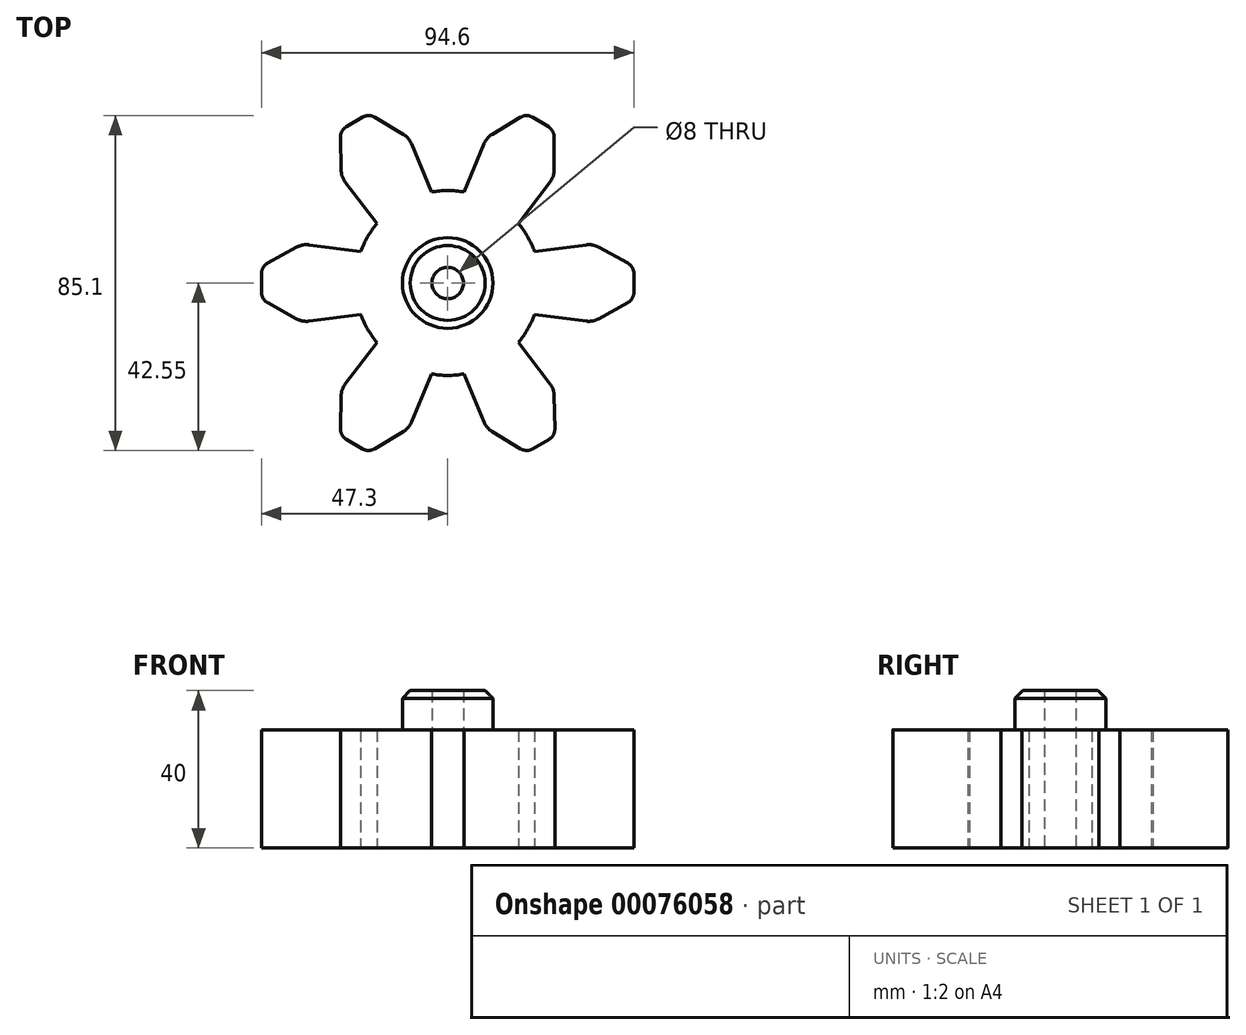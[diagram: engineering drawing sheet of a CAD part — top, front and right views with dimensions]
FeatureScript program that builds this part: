
annotation { "Feature Type Name" : "Feature", "Feature Type Description" : "" }
export const myFeature = defineFeature(function(context is Context, id is Id, definition is map)
    precondition{}
    {
        {
            var Q0;
            Q0=qCreatedBy(makeId("Top.planeOp"),FACE);
            var sketch = newSketch(context, id + "F0", { "sketchPlane" : qUnion([Q0])});
            skCircle(sketch, "E0", {"center": v(0, 0) * mm, "radius": 38.2 * mm, "construction": true});
            skCircle(sketch, "E1", {"center": v(0, 0) * mm, "radius": 50.95 * mm, "construction": true});
            skCircle(sketch, "E2", {"center": v(0, 0) * mm, "radius": 23.47 * mm});
            skLineSegment(sketch, "E3", {"start": v(-50.95, 0) * mm, "end": v(0, 0) * mm});
            skLineSegment(sketch, "E4", {"start": v(0, 0) * mm, "end": v(-25.48, 44.12) * mm, "construction": true});
            skLineSegment(sketch, "E5", {"start": v(0, 0) * mm, "end": v(25.47, 44.12) * mm, "construction": true});
            skLineSegment(sketch, "E6", {"start": v(0, 0) * mm, "end": v(-25.48, -44.12) * mm, "construction": true});
            skLineSegment(sketch, "E7", {"start": v(0, 0) * mm, "end": v(25.48, -44.12) * mm, "construction": true});
            skLineSegment(sketch, "E8", {"start": v(0, 0) * mm, "end": v(50.95, 0) * mm});
            skCircle(sketch, "E9", {"center": v(-19.1, 33.08) * mm, "radius": 10 * mm, "construction": true});
            skCircle(sketch, "E10", {"center": v(-38.2, 0) * mm, "radius": 10 * mm, "construction": true});
            skCircle(sketch, "E11", {"center": v(-19.1, -33.08) * mm, "radius": 10 * mm, "construction": true});
            skCircle(sketch, "E12", {"center": v(19.1, -33.08) * mm, "radius": 10 * mm, "construction": true});
            skCircle(sketch, "E13", {"center": v(38.2, 0) * mm, "radius": 10 * mm, "construction": true});
            skCircle(sketch, "E14", {"center": v(19.1, 33.08) * mm, "radius": 10 * mm, "construction": true});
            skLineSegment(sketch, "E15", {"start": v(0, 0) * mm, "end": v(-44.12, 25.48) * mm, "construction": true});
            skLineSegment(sketch, "E16", {"start": v(0, 0) * mm, "end": v(-44.12, -25.48) * mm, "construction": true});
            skLineSegment(sketch, "E17", {"start": v(-44.12, 25.47) * mm, "end": v(44.12, -25.47) * mm, "construction": true});
            skLineSegment(sketch, "E18", {"start": v(-44.12, -25.47) * mm, "end": v(44.12, 25.47) * mm, "construction": true});
            skLineSegment(sketch, "E19", {"start": v(-27.03, 27) * mm, "end": v(-17.93, 15.14) * mm});
            skLineSegment(sketch, "E20", {"start": v(-9.86, 36.9) * mm, "end": v(-4.15, 23.1) * mm});
            skLineSegment(sketch, "E21", {"start": v(-36.9, 9.91) * mm, "end": v(-22.08, 7.96) * mm});
            skLineSegment(sketch, "E22", {"start": v(-36.9, -9.91) * mm, "end": v(-22.08, -7.96) * mm});
            skLineSegment(sketch, "E23", {"start": v(-27.03, -27) * mm, "end": v(-17.93, -15.14) * mm});
            skLineSegment(sketch, "E24", {"start": v(-9.86, -36.9) * mm, "end": v(-4.15, -23.1) * mm});
            skLineSegment(sketch, "E25", {"start": v(9.86, -36.9) * mm, "end": v(4.15, -23.1) * mm});
            skLineSegment(sketch, "E26", {"start": v(27.03, -27) * mm, "end": v(17.93, -15.14) * mm});
            skLineSegment(sketch, "E27", {"start": v(36.9, -9.91) * mm, "end": v(22.08, -7.96) * mm});
            skLineSegment(sketch, "E28", {"start": v(36.9, 9.91) * mm, "end": v(22.08, 7.96) * mm});
            skLineSegment(sketch, "E29", {"start": v(9.86, 36.9) * mm, "end": v(4.15, 23.1) * mm});
            skLineSegment(sketch, "E30", {"start": v(27.03, 27) * mm, "end": v(17.93, 15.14) * mm});
            skCircle(sketch, "E31", {"center": v(0, 0) * mm, "radius": 4 * mm});
            skCircle(sketch, "E32", {"center": v(-25.48, 44.12) * mm, "radius": 5.53 * mm, "construction": true});
            skLineSegment(sketch, "E33", {"start": v(-27.24, 38.89) * mm, "end": v(-20.06, 43.04) * mm});
            skCircle(sketch, "E34", {"center": v(-50.95, 0) * mm, "radius": 5.53 * mm, "construction": true});
            skCircle(sketch, "E35", {"center": v(-25.48, -44.12) * mm, "radius": 5.53 * mm, "construction": true});
            skCircle(sketch, "E36", {"center": v(25.48, -44.12) * mm, "radius": 5.53 * mm, "construction": true});
            skCircle(sketch, "E37", {"center": v(50.95, 0) * mm, "radius": 5.53 * mm, "construction": true});
            skCircle(sketch, "E38", {"center": v(25.47, 44.12) * mm, "radius": 5.53 * mm, "construction": true});
            skLineSegment(sketch, "E39", {"start": v(-27.24, 38.89) * mm, "end": v(-27.03, 27) * mm});
            skLineSegment(sketch, "E40", {"start": v(-20.06, 43.04) * mm, "end": v(-9.86, 36.9) * mm});
            skLineSegment(sketch, "E41", {"start": v(-36.9, 9.91) * mm, "end": v(-47.3, 4.15) * mm});
            skLineSegment(sketch, "E42", {"start": v(-47.3, -4.15) * mm, "end": v(-36.9, -9.91) * mm});
            skLineSegment(sketch, "E43", {"start": v(-27.24, -38.89) * mm, "end": v(-27.03, -27) * mm});
            skLineSegment(sketch, "E44", {"start": v(-20.06, -43.04) * mm, "end": v(-9.86, -36.9) * mm});
            skLineSegment(sketch, "E45", {"start": v(20.06, -43.04) * mm, "end": v(9.86, -36.9) * mm});
            skLineSegment(sketch, "E46", {"start": v(27.24, -38.89) * mm, "end": v(27.03, -27) * mm});
            skLineSegment(sketch, "E47", {"start": v(47.3, -4.15) * mm, "end": v(36.9, -9.91) * mm});
            skLineSegment(sketch, "E48", {"start": v(47.3, 4.15) * mm, "end": v(36.9, 9.91) * mm});
            skLineSegment(sketch, "E49", {"start": v(27.03, 27) * mm, "end": v(27.03, 38.82) * mm});
            skLineSegment(sketch, "E50", {"start": v(9.86, 36.9) * mm, "end": v(20.06, 43.04) * mm});
            skLineSegment(sketch, "E51", {"start": v(27.03, 38.82) * mm, "end": v(20.06, 43.04) * mm});
            skLineSegment(sketch, "E52", {"start": v(47.3, 4.15) * mm, "end": v(47.3, -4.15) * mm});
            skLineSegment(sketch, "E53", {"start": v(27.24, -38.89) * mm, "end": v(20.06, -43.04) * mm});
            skLineSegment(sketch, "E54", {"start": v(-20.06, -43.04) * mm, "end": v(-27.24, -38.89) * mm});
            skLineSegment(sketch, "E55", {"start": v(-47.3, -4.15) * mm, "end": v(-47.3, 4.15) * mm});
            skCircle(sketch, "E56", {"center": v(0, 0) * mm, "radius": 11.51 * mm});
            skSolve(sketch);
        }
        {
            var Q0;
            {var subQ1=sQuery(id+"F0.wireOp",EDGE,"E19");Q0=makeQuery(id+"F0.imprint","IMPRINT",FACE,{"disambiguationData":[TD([[makeQuery(id+"F0.imprint","IMPRINT",EDGE,{"derivedFrom":subQ1}),1.0]])]});}
            var Q1;
            {var subQ0=sQuery(id+"F0.wireOp",EDGE,"E2");var subQ4=makeQuery(id+"F0.imprint","INTERSECT",VERTEX,{"derivedFrom":[subQ0,sQuery(id+"F0.wireOp",EDGE,"E28")]});Q1=makeQuery(id+"F0.imprint","IMPRINT",FACE,{"disambiguationData":[TD([[makeQuery(id+"F0.imprint","IMPRINT",EDGE,{"disambiguationData":[TD([[subQ4,1.0]])],"derivedFrom":subQ0}),1.0]])]});}
            var Q2;
            {var subQ0=sQuery(id+"F0.wireOp",EDGE,"E2");var subQ9=makeQuery(id+"F0.imprint","INTERSECT",VERTEX,{"derivedFrom":[subQ0,sQuery(id+"F0.wireOp",EDGE,"E22")]});Q2=makeQuery(id+"F0.imprint","IMPRINT",FACE,{"disambiguationData":[TD([[makeQuery(id+"F0.imprint","IMPRINT",EDGE,{"disambiguationData":[TD([[subQ9,1.0]])],"derivedFrom":subQ0}),1.0]])]});}
            var Q3;
            {var subQ6=sQuery(id+"F0.wireOp",EDGE,"E21");Q3=makeQuery(id+"F0.imprint","IMPRINT",FACE,{"disambiguationData":[TD([[makeQuery(id+"F0.imprint","IMPRINT",EDGE,{"derivedFrom":subQ6}),-1.0]])]});}
            var Q4;
            {var subQ1=sQuery(id+"F0.wireOp",EDGE,"E22");Q4=makeQuery(id+"F0.imprint","IMPRINT",FACE,{"disambiguationData":[TD([[makeQuery(id+"F0.imprint","IMPRINT",EDGE,{"derivedFrom":subQ1}),1.0]])]});}
            var Q5;
            {var subQ1=sQuery(id+"F0.wireOp",EDGE,"E23");Q5=makeQuery(id+"F0.imprint","IMPRINT",FACE,{"disambiguationData":[TD([[makeQuery(id+"F0.imprint","IMPRINT",EDGE,{"derivedFrom":subQ1}),-1.0]])]});}
            var Q6;
            {var subQ1=sQuery(id+"F0.wireOp",EDGE,"E25");Q6=makeQuery(id+"F0.imprint","IMPRINT",FACE,{"disambiguationData":[TD([[makeQuery(id+"F0.imprint","IMPRINT",EDGE,{"derivedFrom":subQ1}),-1.0]])]});}
            var Q7;
            {var subQ6=sQuery(id+"F0.wireOp",EDGE,"E27");Q7=makeQuery(id+"F0.imprint","IMPRINT",FACE,{"disambiguationData":[TD([[makeQuery(id+"F0.imprint","IMPRINT",EDGE,{"derivedFrom":subQ6}),-1.0]])]});}
            var Q8;
            {var subQ4=sQuery(id+"F0.wireOp",EDGE,"E28");Q8=makeQuery(id+"F0.imprint","IMPRINT",FACE,{"disambiguationData":[TD([[makeQuery(id+"F0.imprint","IMPRINT",EDGE,{"derivedFrom":subQ4}),1.0]])]});}
            var Q9;
            {var subQ1=sQuery(id+"F0.wireOp",EDGE,"E29");Q9=makeQuery(id+"F0.imprint","IMPRINT",FACE,{"disambiguationData":[TD([[makeQuery(id+"F0.imprint","IMPRINT",EDGE,{"derivedFrom":subQ1}),1.0]])]});}
            var Q10;
            {var subQ0=sQuery(id+"F0.wireOp",EDGE,"E56");var subQ1=sQuery(id+"F0.wireOp",EDGE,"E3");var subQ2=makeQuery(id+"F0.imprint","INTERSECT",VERTEX,{"derivedFrom":[subQ1,subQ0]});Q10=makeQuery(id+"F0.imprint","IMPRINT",FACE,{"disambiguationData":[TD([[makeQuery(id+"F0.imprint","IMPRINT",EDGE,{"disambiguationData":[TD([[subQ2,-1.0]])],"derivedFrom":subQ1}),1.0]])]});}
            var Q11;
            {var subQ0=sQuery(id+"F0.wireOp",EDGE,"E56");var subQ1=sQuery(id+"F0.wireOp",EDGE,"E3");var subQ2=makeQuery(id+"F0.imprint","INTERSECT",VERTEX,{"derivedFrom":[subQ1,subQ0]});Q11=makeQuery(id+"F0.imprint","IMPRINT",FACE,{"disambiguationData":[TD([[makeQuery(id+"F0.imprint","IMPRINT",EDGE,{"disambiguationData":[TD([[subQ2,-1.0]])],"derivedFrom":subQ1}),-1.0]])]});}
            extrude(context, id + "F1", {"entities" : qUnion([Q0, Q1, Q2, Q3, Q4, Q5, Q6, Q7, Q8, Q9, Q10, Q11]), "depth" : 30 * mm});
        }
        {
            var Q0;
            Q0=makeQuery(id+"F1.opExtrude","SWEPT_EDGE",EDGE,{"disambiguationData":[OSD([sQuery(id+"F0.wireOp",EDGE,"E24"),sQuery(id+"F0.wireOp",EDGE,"E44")])]});
            var Q1;
            Q1=makeQuery(id+"F1.opExtrude","SWEPT_EDGE",EDGE,{"disambiguationData":[OSD([sQuery(id+"F0.wireOp",EDGE,"E25"),sQuery(id+"F0.wireOp",EDGE,"E45")])]});
            var Q2;
            Q2=makeQuery(id+"F1.opExtrude","SWEPT_EDGE",EDGE,{"disambiguationData":[OSD([sQuery(id+"F0.wireOp",EDGE,"E26"),sQuery(id+"F0.wireOp",EDGE,"E46")])]});
            var Q3;
            Q3=makeQuery(id+"F1.opExtrude","SWEPT_EDGE",EDGE,{"disambiguationData":[OSD([sQuery(id+"F0.wireOp",EDGE,"E27"),sQuery(id+"F0.wireOp",EDGE,"E47")])]});
            var Q4;
            Q4=makeQuery(id+"F1.opExtrude","SWEPT_EDGE",EDGE,{"disambiguationData":[OSD([sQuery(id+"F0.wireOp",EDGE,"E28"),sQuery(id+"F0.wireOp",EDGE,"E48")])]});
            var Q5;
            Q5=makeQuery(id+"F1.opExtrude","SWEPT_EDGE",EDGE,{"disambiguationData":[OSD([sQuery(id+"F0.wireOp",EDGE,"E30"),sQuery(id+"F0.wireOp",EDGE,"E49")])]});
            var Q6;
            Q6=makeQuery(id+"F1.opExtrude","SWEPT_EDGE",EDGE,{"disambiguationData":[OSD([sQuery(id+"F0.wireOp",EDGE,"E29"),sQuery(id+"F0.wireOp",EDGE,"E50")])]});
            var Q7;
            Q7=makeQuery(id+"F1.opExtrude","SWEPT_EDGE",EDGE,{"disambiguationData":[OSD([sQuery(id+"F0.wireOp",EDGE,"E20"),sQuery(id+"F0.wireOp",EDGE,"E40")])]});
            var Q8;
            Q8=makeQuery(id+"F1.opExtrude","SWEPT_EDGE",EDGE,{"disambiguationData":[OSD([sQuery(id+"F0.wireOp",EDGE,"E19"),sQuery(id+"F0.wireOp",EDGE,"E39")])]});
            var Q9;
            Q9=makeQuery(id+"F1.opExtrude","SWEPT_EDGE",EDGE,{"disambiguationData":[OSD([sQuery(id+"F0.wireOp",EDGE,"E21"),sQuery(id+"F0.wireOp",EDGE,"E41")])]});
            var Q10;
            Q10=makeQuery(id+"F1.opExtrude","SWEPT_EDGE",EDGE,{"disambiguationData":[OSD([sQuery(id+"F0.wireOp",EDGE,"E22"),sQuery(id+"F0.wireOp",EDGE,"E42")])]});
            var Q11;
            Q11=makeQuery(id+"F1.opExtrude","SWEPT_EDGE",EDGE,{"disambiguationData":[OSD([sQuery(id+"F0.wireOp",EDGE,"E23"),sQuery(id+"F0.wireOp",EDGE,"E43")])]});
            fillet(context, id + "F2", {"entities" : qUnion([Q0, Q1, Q2, Q3, Q4, Q5, Q6, Q7, Q8, Q9, Q10, Q11]), "radius" : 5 * mm, "tangentPropagation" : true, "allowEdgeOverflow" : false});
        }
        {
            var Q0;
            Q0=makeQuery(id+"F1.opExtrude","SWEPT_EDGE",EDGE,{"disambiguationData":[OSD([sQuery(id+"F0.wireOp",EDGE,"E42"),sQuery(id+"F0.wireOp",EDGE,"E55")])]});
            var Q1;
            Q1=makeQuery(id+"F1.opExtrude","SWEPT_EDGE",EDGE,{"disambiguationData":[OSD([sQuery(id+"F0.wireOp",EDGE,"E43"),sQuery(id+"F0.wireOp",EDGE,"E54")])]});
            var Q2;
            Q2=makeQuery(id+"F1.opExtrude","SWEPT_EDGE",EDGE,{"disambiguationData":[OSD([sQuery(id+"F0.wireOp",EDGE,"E44"),sQuery(id+"F0.wireOp",EDGE,"E54")])]});
            var Q3;
            Q3=makeQuery(id+"F1.opExtrude","SWEPT_EDGE",EDGE,{"disambiguationData":[OSD([sQuery(id+"F0.wireOp",EDGE,"E45"),sQuery(id+"F0.wireOp",EDGE,"E53")])]});
            var Q4;
            Q4=makeQuery(id+"F1.opExtrude","SWEPT_EDGE",EDGE,{"disambiguationData":[OSD([sQuery(id+"F0.wireOp",EDGE,"E46"),sQuery(id+"F0.wireOp",EDGE,"E53")])]});
            var Q5;
            Q5=makeQuery(id+"F1.opExtrude","SWEPT_EDGE",EDGE,{"disambiguationData":[OSD([sQuery(id+"F0.wireOp",EDGE,"E47"),sQuery(id+"F0.wireOp",EDGE,"E52")])]});
            var Q6;
            Q6=makeQuery(id+"F1.opExtrude","SWEPT_EDGE",EDGE,{"disambiguationData":[OSD([sQuery(id+"F0.wireOp",EDGE,"E48"),sQuery(id+"F0.wireOp",EDGE,"E52")])]});
            var Q7;
            Q7=makeQuery(id+"F1.opExtrude","SWEPT_EDGE",EDGE,{"disambiguationData":[OSD([sQuery(id+"F0.wireOp",EDGE,"E49"),sQuery(id+"F0.wireOp",EDGE,"E51")])]});
            var Q8;
            Q8=makeQuery(id+"F1.opExtrude","SWEPT_EDGE",EDGE,{"disambiguationData":[OSD([sQuery(id+"F0.wireOp",EDGE,"E50"),sQuery(id+"F0.wireOp",EDGE,"E51")])]});
            var Q9;
            Q9=makeQuery(id+"F1.opExtrude","SWEPT_EDGE",EDGE,{"disambiguationData":[OSD([sQuery(id+"F0.wireOp",EDGE,"E33"),sQuery(id+"F0.wireOp",EDGE,"E40")])]});
            var Q10;
            Q10=makeQuery(id+"F1.opExtrude","SWEPT_EDGE",EDGE,{"disambiguationData":[OSD([sQuery(id+"F0.wireOp",EDGE,"E33"),sQuery(id+"F0.wireOp",EDGE,"E39")])]});
            var Q11;
            Q11=makeQuery(id+"F1.opExtrude","SWEPT_EDGE",EDGE,{"disambiguationData":[OSD([sQuery(id+"F0.wireOp",EDGE,"E41"),sQuery(id+"F0.wireOp",EDGE,"E55")])]});
            fillet(context, id + "F3", {"entities" : qUnion([Q0, Q1, Q2, Q3, Q4, Q5, Q6, Q7, Q8, Q9, Q10, Q11]), "radius" : 3 * mm, "tangentPropagation" : true, "allowEdgeOverflow" : false});
        }
        {
            var Q0;
            {var subQ0=sQuery(id+"F0.wireOp",EDGE,"E56");var subQ1=sQuery(id+"F0.wireOp",EDGE,"E3");var subQ2=makeQuery(id+"F0.imprint","INTERSECT",VERTEX,{"derivedFrom":[subQ1,subQ0]});Q0=makeQuery(id+"F0.imprint","IMPRINT",FACE,{"disambiguationData":[TD([[makeQuery(id+"F0.imprint","IMPRINT",EDGE,{"disambiguationData":[TD([[subQ2,-1.0]])],"derivedFrom":subQ1}),-1.0]])]});}
            var Q1;
            {var subQ0=sQuery(id+"F0.wireOp",EDGE,"E56");var subQ1=sQuery(id+"F0.wireOp",EDGE,"E3");var subQ2=makeQuery(id+"F0.imprint","INTERSECT",VERTEX,{"derivedFrom":[subQ1,subQ0]});Q1=makeQuery(id+"F0.imprint","IMPRINT",FACE,{"disambiguationData":[TD([[makeQuery(id+"F0.imprint","IMPRINT",EDGE,{"disambiguationData":[TD([[subQ2,-1.0]])],"derivedFrom":subQ1}),1.0]])]});}
            extrude(context, id + "F4", {"entities" : qUnion([Q0, Q1]), "operationType" : NewBodyOperationType.ADD, "depth" : 40 * mm});
        }
        {
            var Q0;
            Q0=makeQuery(id+"F4.opExtrude","CAP_EDGE",EDGE,{"disambiguationData":[OSD([sQuery(id+"F0.wireOp",EDGE,"E56")])],"isStart":false});
            chamfer(context, id + "F5", {"entities" : qUnion([Q0]), "width" : 2 * mm, "tangentPropagation" : true});
        }
    });
